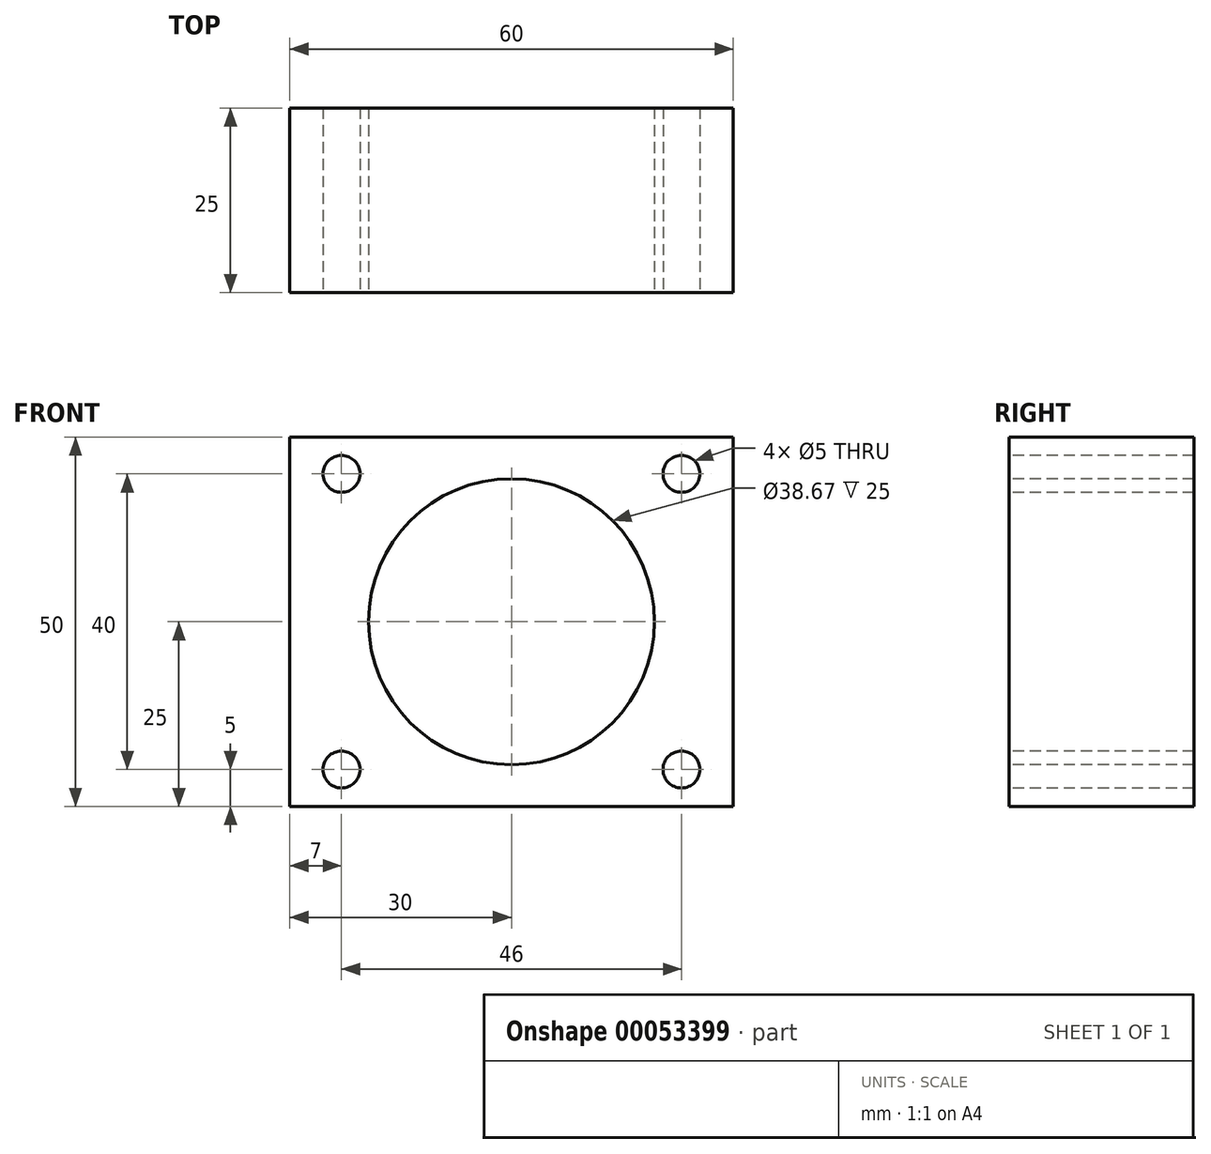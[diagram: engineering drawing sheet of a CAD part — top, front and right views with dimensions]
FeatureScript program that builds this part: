
annotation { "Feature Type Name" : "Feature", "Feature Type Description" : "" }
export const myFeature = defineFeature(function(context is Context, id is Id, definition is map)
    precondition{}
    {
        {
            var Q0;
            Q0=qCreatedBy(makeId("Front.planeOp"),FACE);
            var sketch = newSketch(context, id + "F0", { "sketchPlane" : qUnion([Q0])});
            skLineSegment(sketch, "E0.rect.bottom", {"start": v(30, -25) * mm, "end": v(-30, -25) * mm});
            skLineSegment(sketch, "E0.rect.top", {"start": v(30, 25) * mm, "end": v(-30, 25) * mm});
            skLineSegment(sketch, "E0.rect.left", {"start": v(30, -25) * mm, "end": v(30, 25) * mm});
            skLineSegment(sketch, "E0.rect.right", {"start": v(-30, -25) * mm, "end": v(-30, 25) * mm});
            skPoint(sketch, "E0.rect.middle", {"position": v(0, 0) * mm});
            skSolve(sketch);
        }
        {
            var Q0;
            Q0 = qSketchRegion(id + "F0", true);
            extrude(context, id + "F1", {"entities" : qUnion([Q0]), "depth" : 25 * mm});
        }
        {
            var Q0;
            Q0=makeQuery(id+"F1.opExtrude","CAP_FACE",FACE,{"disambiguationData":[OSD([sQuery(id+"F0.wireOp",EDGE,"E0.rect.bottom"),sQuery(id+"F0.wireOp",EDGE,"E0.rect.top"),sQuery(id+"F0.wireOp",EDGE,"E0.rect.left"),sQuery(id+"F0.wireOp",EDGE,"E0.rect.right")])],"isStart":false});
            var sketch = newSketch(context, id + "F2", { "sketchPlane" : qUnion([Q0])});
            skCircle(sketch, "E1", {"center": v(-23, 20) * mm, "radius": 2.5 * mm});
            skCircle(sketch, "E2", {"center": v(23, 20) * mm, "radius": 2.5 * mm});
            skCircle(sketch, "E3", {"center": v(-23, -20) * mm, "radius": 2.5 * mm});
            skCircle(sketch, "E4", {"center": v(23, -20) * mm, "radius": 2.5 * mm});
            skCircle(sketch, "E5", {"center": v(0, 0) * mm, "radius": 19.34 * mm});
            skSolve(sketch);
        }
        {
            var Q0;
            Q0 = qSketchRegion(id + "F2", true);
            extrude(context, id + "F3", {"entities" : qUnion([Q0]), "operationType" : NewBodyOperationType.REMOVE, "endBound" : BoundingType.THROUGH_ALL, "oppositeDirection" : true, "depth" : 25 * mm});
        }
    });
